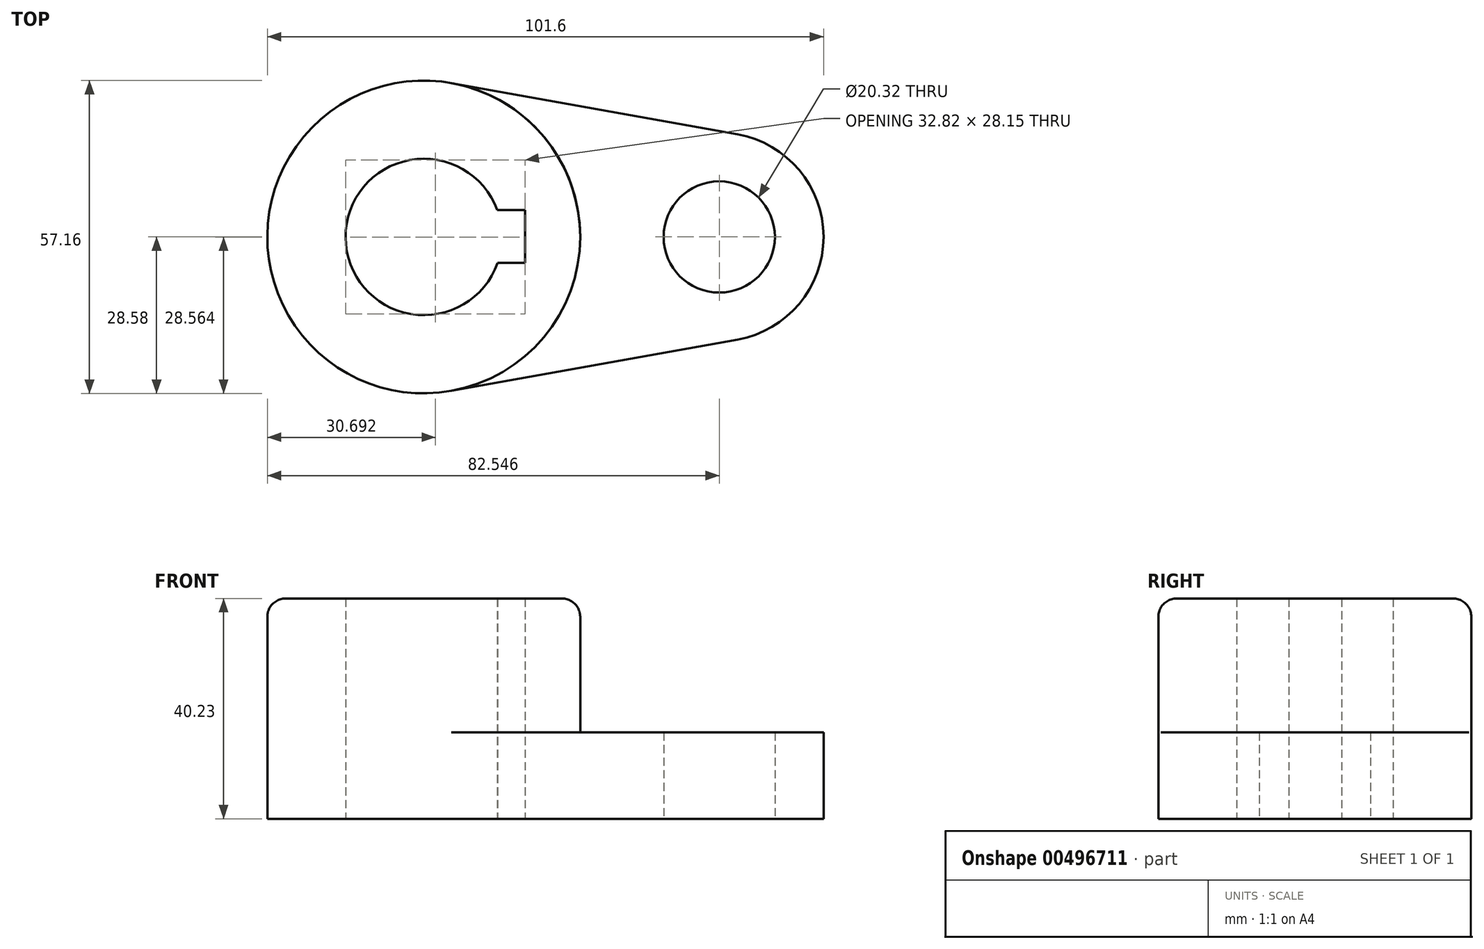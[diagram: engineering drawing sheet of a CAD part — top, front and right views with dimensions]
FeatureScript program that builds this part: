
annotation { "Feature Type Name" : "Feature", "Feature Type Description" : "" }
export const myFeature = defineFeature(function(context is Context, id is Id, definition is map)
    precondition{}
    {
        {
            var Q0;
            Q0=qCreatedBy(makeId("Top.planeOp"),FACE);
            var sketch = newSketch(context, id + "F0", { "sketchPlane" : qUnion([Q0])});
            skCircle(sketch, "E0", {"center": v(-31.25, 0) * mm, "radius": 28.58 * mm});
            skArc(sketch, "E1", {"start": v(26.09, -18.75) * mm, "mid": v(41.78, 0) * mm, "end": v(26.09, 18.75) * mm});
            skLineSegment(sketch, "E2", {"start": v(-26.2, 28.13) * mm, "end": v(26.09, 18.75) * mm});
            skLineSegment(sketch, "E3", {"start": v(-26.2, -28.13) * mm, "end": v(26.09, -18.75) * mm});
            skCircle(sketch, "E4", {"center": v(22.73, 0) * mm, "radius": 10.16 * mm});
            skArc(sketch, "E5", {"start": v(-17.83, 4.91) * mm, "mid": v(-45.54, -0.1) * mm, "end": v(-17.77, -4.74) * mm});
            skLineSegment(sketch, "E6", {"start": v(-17.83, 4.91) * mm, "end": v(-12.72, 4.91) * mm});
            skLineSegment(sketch, "E7", {"start": v(-12.72, 4.91) * mm, "end": v(-12.72, -4.74) * mm});
            skLineSegment(sketch, "E8", {"start": v(-12.72, -4.74) * mm, "end": v(-17.77, -4.74) * mm});
            skSolve(sketch);
        }
        {
            var Q0;
            Q0=makeQuery(id+"F0.imprint","IMPRINT",FACE,{"disambiguationData":[TD([[makeQuery(id+"F0.imprint","IMPRINT",EDGE,{"derivedFrom":sQuery(id+"F0.wireOp",EDGE,"E5")}),-1.0]])]});
            extrude(context, id + "F1", {"entities" : qUnion([Q0]), "depth" : 40.23 * mm});
        }
        {
            var Q0;
            Q0=makeQuery(id+"F1.opExtrude","CAP_EDGE",EDGE,{"disambiguationData":[OSD([sQuery(id+"F0.wireOp",EDGE,"E0")])],"isStart":false});
            fillet(context, id + "F2", {"entities" : qUnion([Q0]), "radius" : 3.3 * mm, "tangentPropagation" : true, "allowEdgeOverflow" : false});
        }
        {
            var Q0;
            Q0=makeQuery(id+"F0.imprint","IMPRINT",FACE,{"disambiguationData":[TD([[makeQuery(id+"F0.imprint","IMPRINT",EDGE,{"derivedFrom":sQuery(id+"F0.wireOp",EDGE,"E1")}),1.0]])]});
            extrude(context, id + "F3", {"entities" : qUnion([Q0]), "operationType" : NewBodyOperationType.ADD, "depth" : 15.77 * mm});
        }
    });
